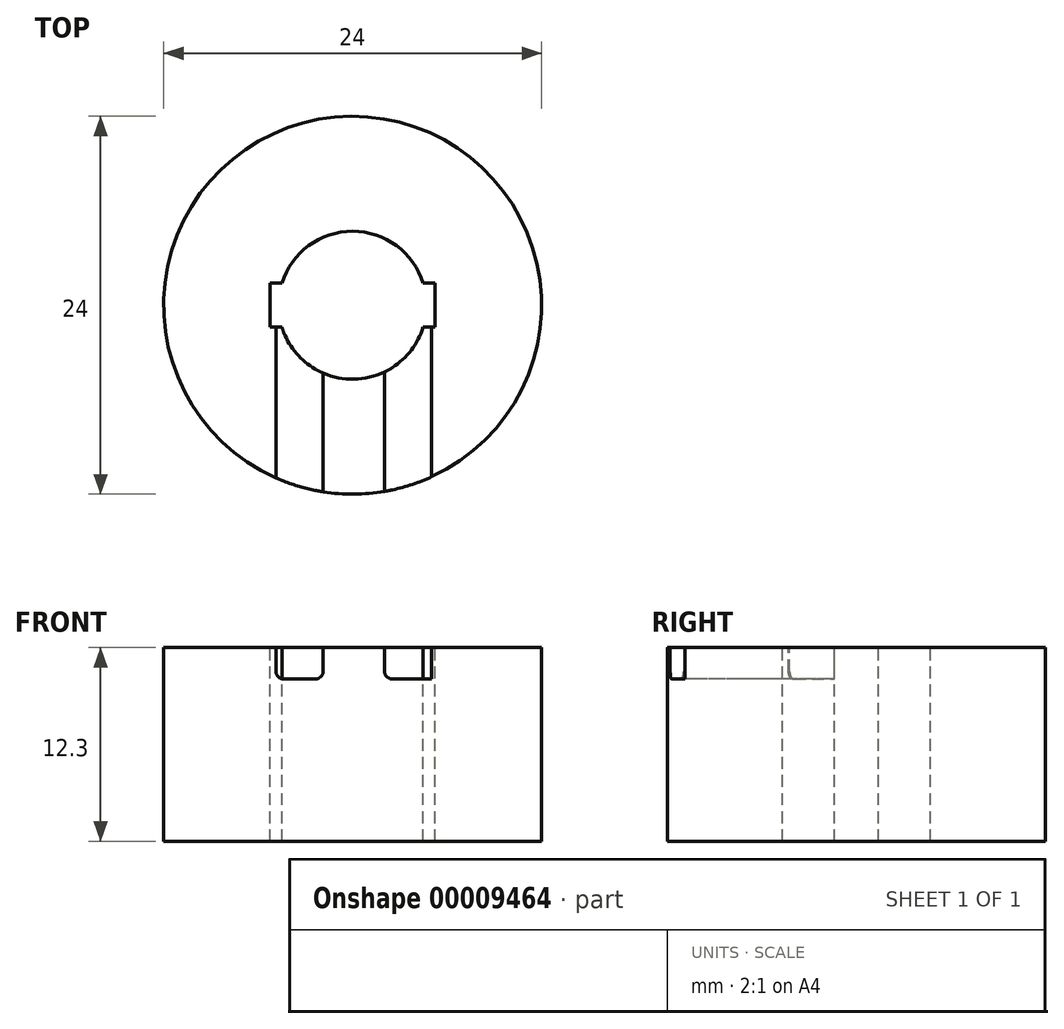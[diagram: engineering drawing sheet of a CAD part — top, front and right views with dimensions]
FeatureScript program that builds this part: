
annotation { "Feature Type Name" : "Feature", "Feature Type Description" : "" }
export const myFeature = defineFeature(function(context is Context, id is Id, definition is map)
    precondition{}
    {
        {
            var Q0;
            Q0=qCreatedBy(makeId("Top.planeOp"),FACE);
            var sketch = newSketch(context, id + "F0", { "sketchPlane" : qUnion([Q0])});
            skCircle(sketch, "E0", {"center": v(0, 0) * mm, "radius": 12 * mm});
            skSolve(sketch);
        }
        {
            var Q0;
            Q0 = qSketchRegion(id + "F0", true);
            extrude(context, id + "F1", {"entities" : qUnion([Q0]), "depth" : 12.3 * mm});
        }
        {
            var Q0;
            Q0=makeQuery(id+"F1.opExtrude","CAP_FACE",FACE,{"disambiguationData":[OSD([sQuery(id+"F0.wireOp",EDGE,"E0")])],"isStart":false});
            var sketch = newSketch(context, id + "F2", { "sketchPlane" : qUnion([Q0])});
            skArc(sketch, "E1", {"start": v(-4.49, -1.4) * mm, "mid": v(0, -4.7) * mm, "end": v(4.49, -1.4) * mm});
            skLineSegment(sketch, "E2.rect.bottom", {"start": v(5.25, -1.4) * mm, "end": v(4.49, -1.4) * mm});
            skLineSegment(sketch, "E2.rect.top", {"start": v(5.25, 1.4) * mm, "end": v(4.49, 1.4) * mm});
            skLineSegment(sketch, "E2.rect.left", {"start": v(5.25, -1.4) * mm, "end": v(5.25, 1.4) * mm});
            skLineSegment(sketch, "E2.rect.right", {"start": v(-5.25, -1.4) * mm, "end": v(-5.25, 1.4) * mm});
            skLineSegment(sketch, "E3.trimOffspring", {"start": v(-4.49, 1.4) * mm, "end": v(-5.25, 1.4) * mm});
            skLineSegment(sketch, "E4.trimOffspring", {"start": v(-4.49, -1.4) * mm, "end": v(-5.25, -1.4) * mm});
            skArc(sketch, "E5.trimOffspring", {"start": v(4.49, 1.4) * mm, "mid": v(0, 4.7) * mm, "end": v(-4.49, 1.4) * mm});
            skSolve(sketch);
        }
        {
            var Q0;
            Q0=makeQuery(id+"F2.imprint","IMPRINT",FACE,{"disambiguationData":[TD([[makeQuery(id+"F2.imprint","IMPRINT",EDGE,{"derivedFrom":sQuery(id+"F2.wireOp",EDGE,"E1")}),1.0]])]});
            extrude(context, id + "F3", {"entities" : qUnion([Q0]), "operationType" : NewBodyOperationType.REMOVE, "oppositeDirection" : true, "depth" : 25 * mm});
        }
        {
            var Q0;
            Q0=makeQuery(id+"F1.opExtrude","CAP_FACE",FACE,{"disambiguationData":[OSD([sQuery(id+"F0.wireOp",EDGE,"E0")])],"isStart":false});
            var sketch = newSketch(context, id + "F4", { "sketchPlane" : qUnion([Q0])});
            skLineSegment(sketch, "E6.bottom", {"start": v(5.03, -1.32) * mm, "end": v(2.03, -1.32) * mm});
            skLineSegment(sketch, "E6.top", {"start": v(5.03, -12.88) * mm, "end": v(2.03, -12.88) * mm});
            skLineSegment(sketch, "E6.left", {"start": v(5.03, -1.32) * mm, "end": v(5.03, -12.88) * mm});
            skLineSegment(sketch, "E6.right", {"start": v(2.03, -1.32) * mm, "end": v(2.03, -12.88) * mm});
            skLineSegment(sketch, "E7.bottom", {"start": v(-4.87, -1.4) * mm, "end": v(-1.87, -1.4) * mm});
            skLineSegment(sketch, "E7.top", {"start": v(-4.87, -13.35) * mm, "end": v(-1.87, -13.35) * mm});
            skLineSegment(sketch, "E7.left", {"start": v(-4.87, -1.4) * mm, "end": v(-4.87, -13.35) * mm});
            skLineSegment(sketch, "E7.right", {"start": v(-1.87, -1.4) * mm, "end": v(-1.87, -13.35) * mm});
            skSolve(sketch);
        }
        {
            var Q0;
            Q0 = qSketchRegion(id + "F4", true);
            extrude(context, id + "F5", {"entities" : qUnion([Q0]), "operationType" : NewBodyOperationType.REMOVE, "oppositeDirection" : true, "depth" : 2 * mm});
        }
        {
            var Q0;
            Q0=makeQuery(id+"F5.boolean.opBoolean","COPY",EDGE,{"derivedFrom":makeQuery(id+"F5.opExtrude","CAP_EDGE",EDGE,{"disambiguationData":[OSD([sQuery(id+"F4.wireOp",EDGE,"E7.right")])],"isStart":false})});
            var Q1;
            Q1=makeQuery(id+"F5.boolean.opBoolean","COPY",EDGE,{"derivedFrom":makeQuery(id+"F5.opExtrude","CAP_EDGE",EDGE,{"disambiguationData":[OSD([sQuery(id+"F4.wireOp",EDGE,"E7.left")])],"isStart":false})});
            var Q2;
            Q2=makeQuery(id+"F5.boolean.opBoolean","COPY",EDGE,{"derivedFrom":makeQuery(id+"F5.opExtrude","CAP_EDGE",EDGE,{"disambiguationData":[OSD([sQuery(id+"F4.wireOp",EDGE,"E6.right")])],"isStart":false})});
            fillet(context, id + "F6", {"entities" : qUnion([Q0, Q1, Q2]), "radius" : 0.5 * mm, "tangentPropagation" : true, "allowEdgeOverflow" : false});
        }
    });
